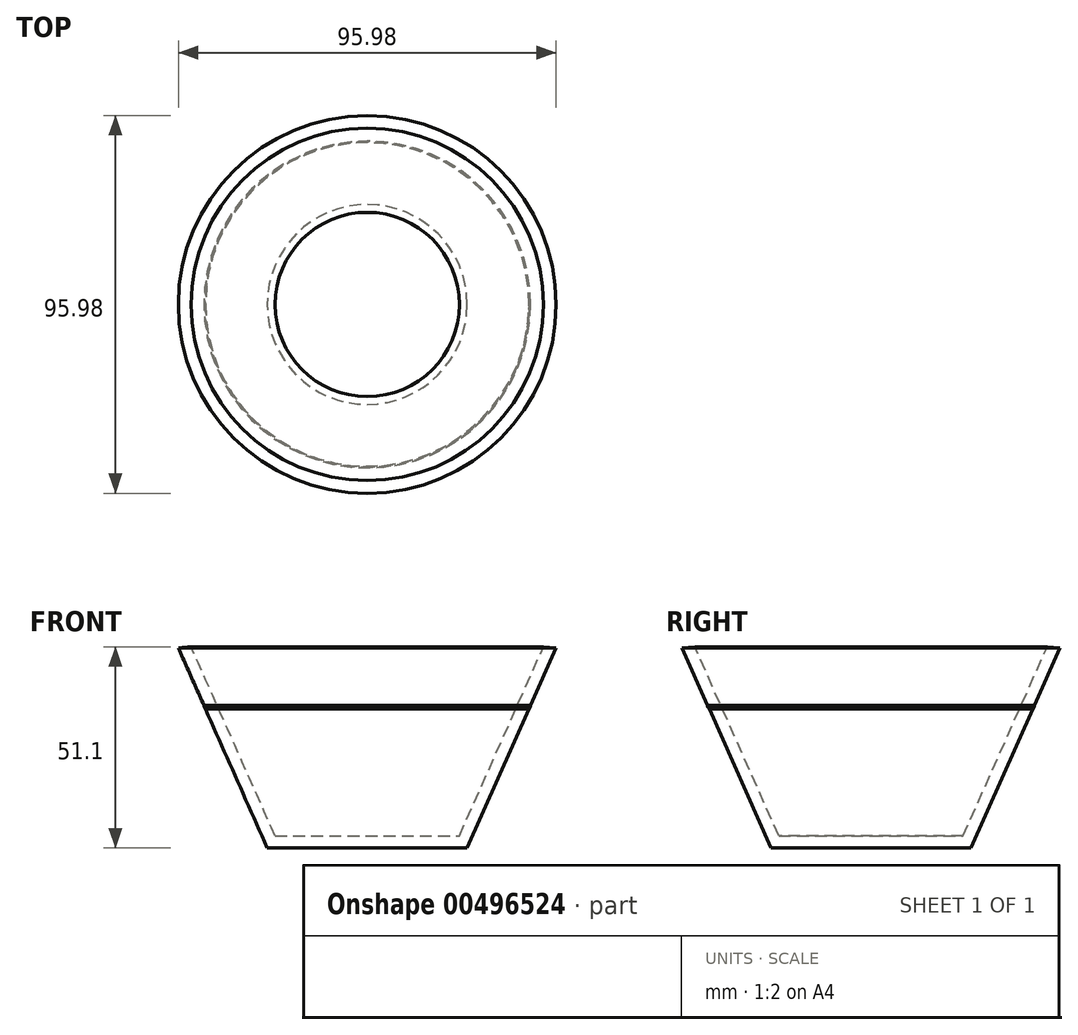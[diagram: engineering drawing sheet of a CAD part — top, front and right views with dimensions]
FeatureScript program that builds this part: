
annotation { "Feature Type Name" : "Feature", "Feature Type Description" : "" }
export const myFeature = defineFeature(function(context is Context, id is Id, definition is map)
    precondition{}
    {
        {
            var Q0;
            Q0=qCreatedBy(makeId("Front.planeOp"),FACE);
            var sketch = newSketch(context, id + "F0", { "sketchPlane" : qUnion([Q0])});
            skLineSegment(sketch, "E0", {"start": v(0, 0) * mm, "end": v(0, 50.8) * mm, "construction": true});
            skLineSegment(sketch, "E1", {"start": v(0, 0) * mm, "end": v(25.4, 0) * mm});
            skLineSegment(sketch, "E2", {"start": v(25.4, 0) * mm, "end": v(47.99, 50.8) * mm});
            skLineSegment(sketch, "E3.0", {"start": v(23.4, 3.07) * mm, "end": v(44.76, 51.1) * mm});
            skLineSegment(sketch, "E3.1", {"start": v(-0.4, 3.07) * mm, "end": v(23.4, 3.07) * mm});
            skLineSegment(sketch, "E4", {"start": v(47.99, 50.8) * mm, "end": v(44.76, 51.1) * mm});
            skLineSegment(sketch, "E5", {"start": v(0, 0) * mm, "end": v(0, 3.07) * mm});
            skLineSegment(sketch, "E6", {"start": v(41.48, 36.17) * mm, "end": v(41.48, 35.86) * mm});
            skLineSegment(sketch, "E7", {"start": v(41.48, 35.86) * mm, "end": v(41.35, 35.86) * mm});
            skLineSegment(sketch, "E8", {"start": v(41.35, 35.86) * mm, "end": v(41.35, 35.59) * mm});
            skLineSegment(sketch, "E9", {"start": v(41.35, 35.59) * mm, "end": v(41.22, 35.59) * mm});
            skLineSegment(sketch, "E10", {"start": v(41.22, 35.59) * mm, "end": v(41.22, 35.27) * mm});
            skLineSegment(sketch, "E11", {"start": v(41.22, 35.27) * mm, "end": v(41.08, 35.27) * mm});
            skSolve(sketch);
        }
        {
            var Q0;
            Q0=makeQuery(id+"F0.imprint","IMPRINT",FACE,{"disambiguationData":[TD([[makeQuery(id+"F0.imprint","IMPRINT",EDGE,{"derivedFrom":sQuery(id+"F0.wireOp",EDGE,"E1")}),1.0]])]});
            var Q1;
            {var subQ0=sQuery(id+"F0.wireOp",EDGE,"sAYKoBsH-cj0b-eDUG-5M8L-M0liTHtloDEJ");Q1=makeQuery(id+"F0.imprint","IMPRINT",FACE,{"disambiguationData":[TD([[makeQuery(id+"F0.imprint","IMPRINT",EDGE,{"derivedFrom":subQ0}),-1.0]])]});}
            var Q2;
            {var subQ0=sQuery(id+"F0.wireOp",EDGE,"87mYQOYL-Nmvj-nmlh-2ZrG-IztUeHGoN2Ih");Q2=makeQuery(id+"F0.imprint","IMPRINT",FACE,{"disambiguationData":[TD([[makeQuery(id+"F0.imprint","IMPRINT",EDGE,{"derivedFrom":subQ0}),-1.0]])]});}
            var Q3;
            {var subQ0=sQuery(id+"F0.wireOp",EDGE,"s3wjUbq9-Ir5T-hr7K-ssRO-WLh3rWFXYiNl");Q3=makeQuery(id+"F0.imprint","IMPRINT",FACE,{"disambiguationData":[TD([[makeQuery(id+"F0.imprint","IMPRINT",EDGE,{"derivedFrom":subQ0}),-1.0]])]});}
            var Q4;
            {var subQ0=sQuery(id+"F0.wireOp",EDGE,"E6");Q4=makeQuery(id+"F0.imprint","IMPRINT",FACE,{"disambiguationData":[TD([[makeQuery(id+"F0.imprint","IMPRINT",EDGE,{"derivedFrom":subQ0}),-1.0]])]});}
            var Q5;
            {var subQ0=sQuery(id+"F0.wireOp",EDGE,"E8");Q5=makeQuery(id+"F0.imprint","IMPRINT",FACE,{"disambiguationData":[TD([[makeQuery(id+"F0.imprint","IMPRINT",EDGE,{"derivedFrom":subQ0}),-1.0]])]});}
            var Q6;
            {var subQ0=sQuery(id+"F0.wireOp",EDGE,"E10");Q6=makeQuery(id+"F0.imprint","IMPRINT",FACE,{"disambiguationData":[TD([[makeQuery(id+"F0.imprint","IMPRINT",EDGE,{"derivedFrom":subQ0}),-1.0]])]});}
            var Q7;
            Q7=sQuery(id+"F0.wireOp",EDGE,"E0");
            revolve(context, id + "F1", {"entities" : qUnion([Q0, Q1, Q2, Q3, Q4, Q5, Q6]), "axis" : qUnion([Q7]), "revolveType" : RevolveType.FULL});
        }
    });
